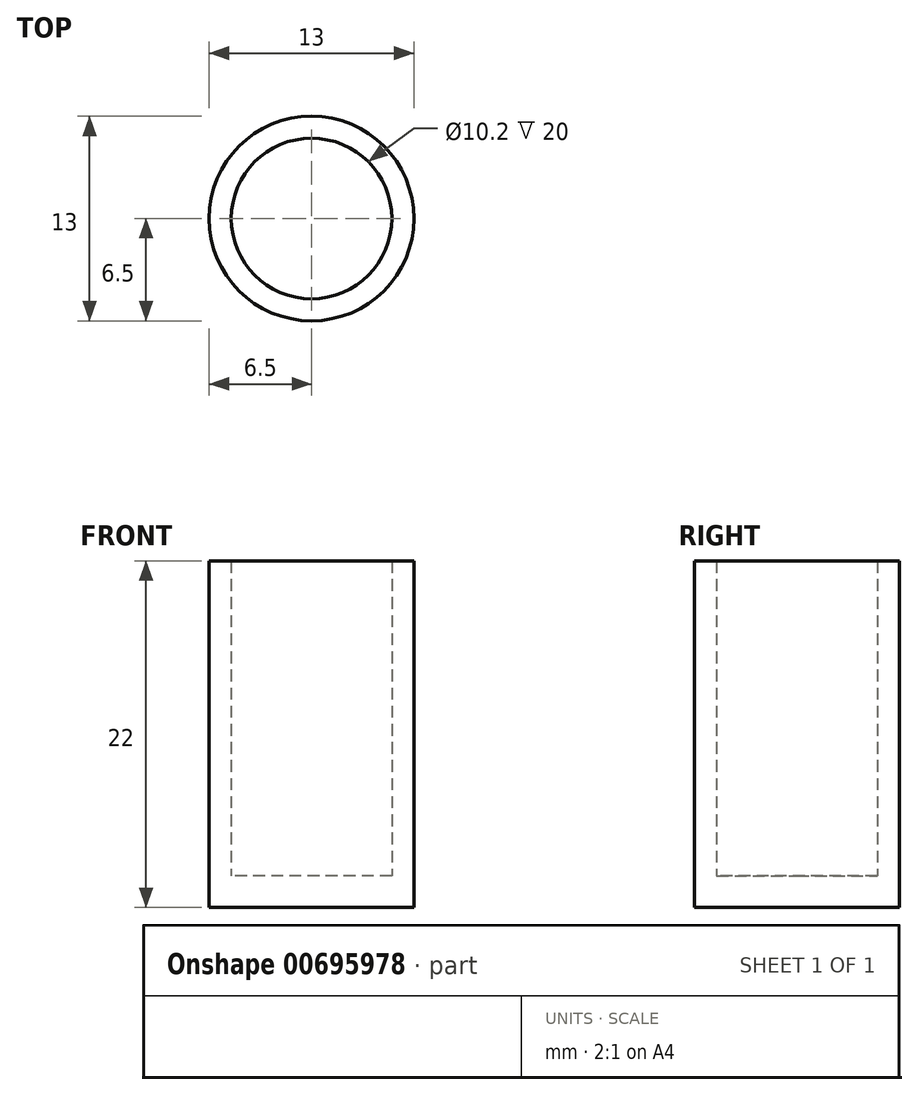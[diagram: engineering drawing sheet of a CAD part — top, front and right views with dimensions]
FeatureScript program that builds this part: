
annotation { "Feature Type Name" : "Feature", "Feature Type Description" : "" }
export const myFeature = defineFeature(function(context is Context, id is Id, definition is map)
    precondition{}
    {
        {
            var Q0;
            Q0=qCreatedBy(makeId("Top.planeOp"),FACE);
            var sketch = newSketch(context, id + "F0", { "sketchPlane" : qUnion([Q0])});
            skCircle(sketch, "E0", {"center": v(0, 0) * mm, "radius": 5.1 * mm});
            skSolve(sketch);
        }
        {
            var Q0;
            Q0=qCreatedBy(makeId("Top.planeOp"),FACE);
            var sketch = newSketch(context, id + "F1", { "sketchPlane" : qUnion([Q0])});
            skCircle(sketch, "E1", {"center": v(0, 0) * mm, "radius": 6.5 * mm});
            skSolve(sketch);
        }
        {
            var Q0;
            Q0 = qSketchRegion(id + "F1", true);
            extrude(context, id + "F2", {"entities" : qUnion([Q0]), "depth" : 22 * mm, "offsetDistance" : 25 * mm});
        }
        {
            var Q0;
            Q0 = qSketchRegion(id + "F0", true);
            extrude(context, id + "F3", {"entities" : qUnion([Q0]), "operationType" : NewBodyOperationType.REMOVE, "depth" : 22 * mm, "offsetDistance" : 25 * mm, "hasSecondDirection" : true, "secondDirectionOppositeDirection" : true, "secondDirectionDepth" : -2 * mm});
        }
    });
